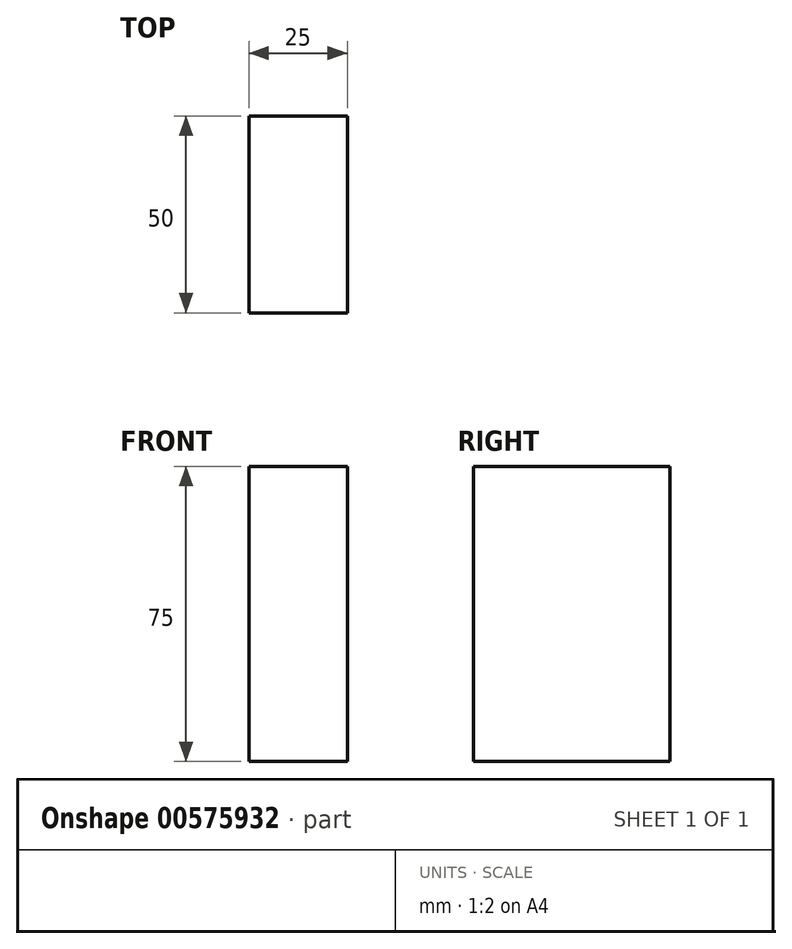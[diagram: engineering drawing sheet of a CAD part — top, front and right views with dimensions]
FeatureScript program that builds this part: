
annotation { "Feature Type Name" : "Feature", "Feature Type Description" : "" }
export const myFeature = defineFeature(function(context is Context, id is Id, definition is map)
    precondition{}
    {
        {
            var Q0;
            Q0=qCreatedBy(makeId("Top.planeOp"),FACE);
            var sketch = newSketch(context, id + "F0", { "sketchPlane" : qUnion([Q0])});
            skLineSegment(sketch, "E0.bottom", {"start": v(0, 0) * mm, "end": v(25, 0) * mm});
            skLineSegment(sketch, "E0.top", {"start": v(0, 50) * mm, "end": v(25, 50) * mm});
            skLineSegment(sketch, "E0.left", {"start": v(0, 0) * mm, "end": v(0, 50) * mm});
            skLineSegment(sketch, "E0.right", {"start": v(25, 0) * mm, "end": v(25, 50) * mm});
            skSolve(sketch);
        }
        {
            var Q0;
            Q0 = qSketchRegion(id + "F0", true);
            var Q1;
            Q1=makeQuery(id+"F0.imprint","IMPRINT",FACE,{"disambiguationData":[TD([[makeQuery(id+"F0.imprint","IMPRINT",EDGE,{"derivedFrom":sQuery(id+"F0.wireOp",EDGE,"E0.bottom")}),1.0]])]});
            extrude(context, id + "F1", {"entities" : qUnion([Q0, Q1]), "depth" : 75 * mm, "offsetDistance" : 25 * mm});
        }
    });
